# Revit family: Cube
name_source: partatom
category: Furniture
units: mm (PartAtom-declared; Revit-internal decimal feet)

## family parameters
Always vertical = Yes
Cut with Voids When Loaded = No
OmniClass Number = 23.40.00.00
OmniClass Title = Equipment and Furnishings
Room Calculation Point = No
Shared = No
Work Plane-Based = No

## types (3) — shared parameters
Assembly Code = E2020200
Manufacturer = Gresham Office Funiture
Model = CUBE
Range = SEATING
Seat = Gresham - Blue Fabric
URL = www.gof.co.uk

## per-type parameters (varying)
| type | Base Height | Castors | Glides | Legs |
| ES01 | 25 mm  [stored 0.082021 ft] | No | Yes | No |
| ES01C | 72 mm  [stored 0.23622 ft] | Yes | No | No |
| ES01M | 100 mm  [stored 0.328084 ft] | No | No | Yes |

note: column(s) folded — value = type name in every type: Product Code

note: [stored X ft] marks values corroborated as IEEE doubles in the binary element streams (Revit-internal decimal feet)

## geometry (parser evidence)
native form markers: Blend x2, Sweep x12
no freeform markers — native parametric forms only
